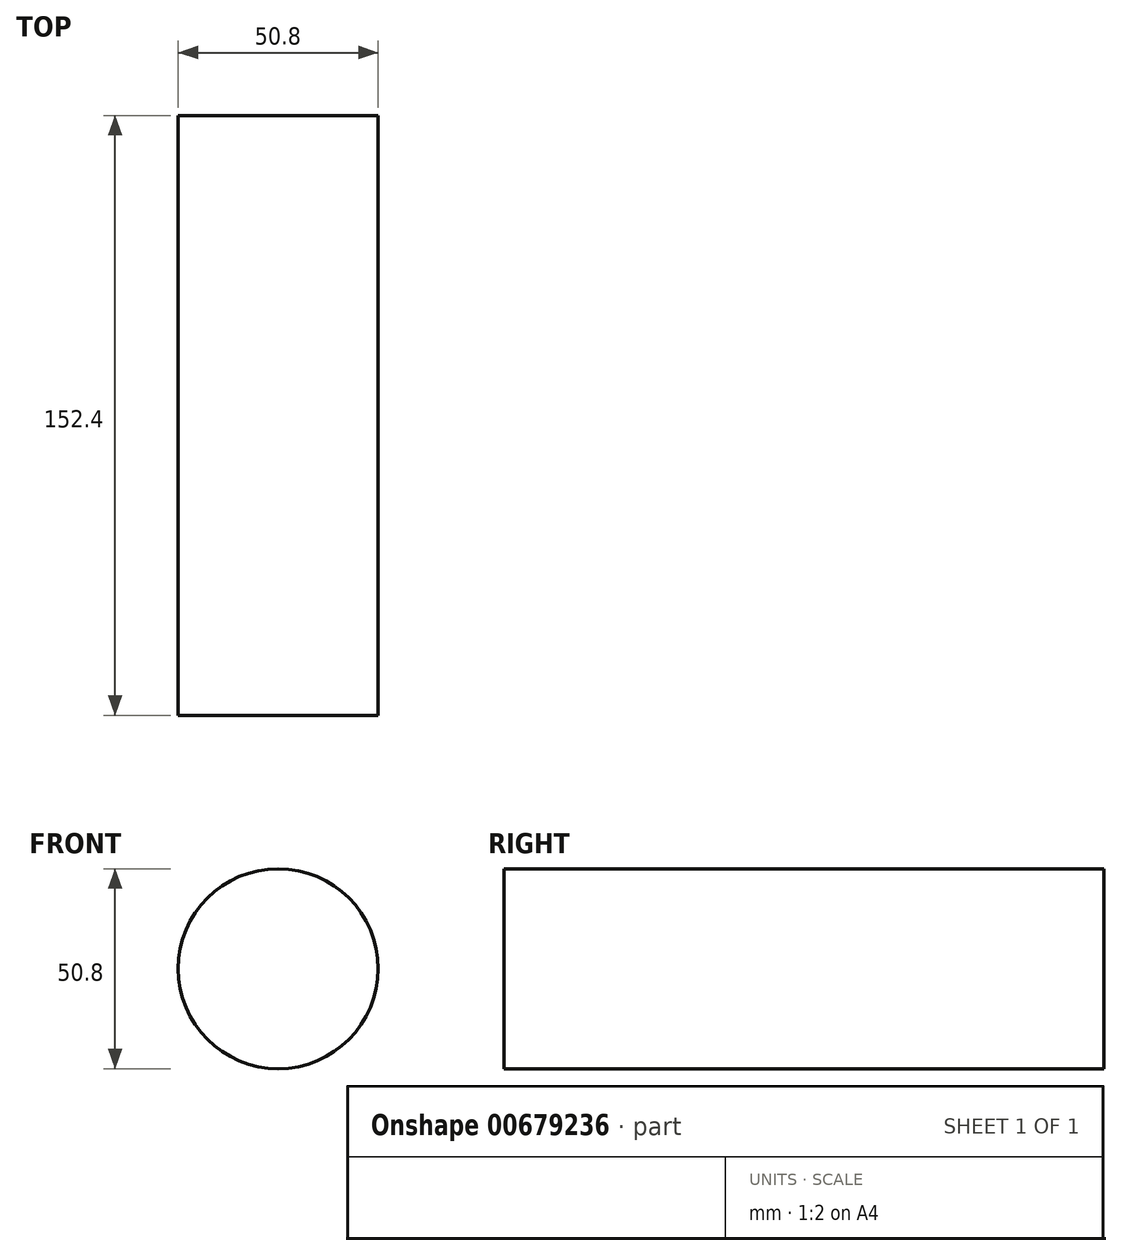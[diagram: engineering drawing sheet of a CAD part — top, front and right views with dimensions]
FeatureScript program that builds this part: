
annotation { "Feature Type Name" : "Feature", "Feature Type Description" : "" }
export const myFeature = defineFeature(function(context is Context, id is Id, definition is map)
    precondition{}
    {
        {
            var Q0;
            Q0=qCreatedBy(makeId("Front.planeOp"),FACE);
            var sketch = newSketch(context, id + "F0", { "sketchPlane" : qUnion([Q0])});
            skCircle(sketch, "E0", {"center": v(0, 0) * mm, "radius": 25.4 * mm});
            skSolve(sketch);
        }
        {
            var Q0;
            Q0 = qSketchRegion(id + "F0", true);
            extrude(context, id + "F1", {"entities" : qUnion([Q0]), "endBound" : BoundingType.SYMMETRIC, "depth" : 152.4 * mm, "offsetDistance" : 25.4 * mm});
        }
    });
